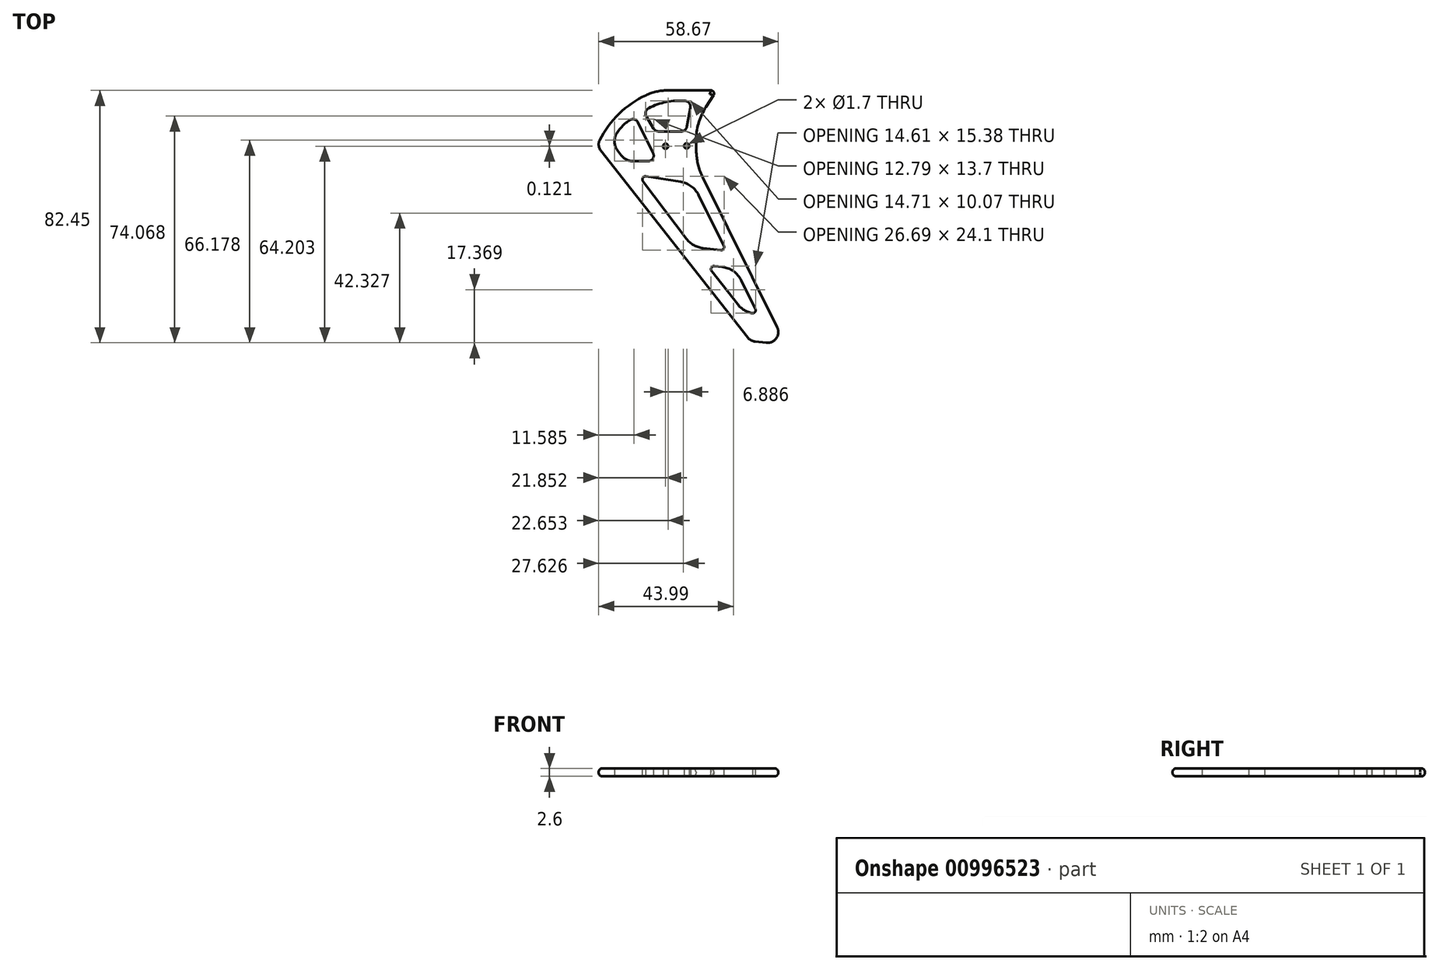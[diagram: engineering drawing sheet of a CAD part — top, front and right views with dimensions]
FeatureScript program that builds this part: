
annotation { "Feature Type Name" : "Feature", "Feature Type Description" : "" }
export const myFeature = defineFeature(function(context is Context, id is Id, definition is map)
    precondition{}
    {
        {
            var Q0;
            Q0=qCreatedBy(makeId("Top.planeOp"),FACE);
            var sketch = newSketch(context, id + "F0", { "sketchPlane" : qUnion([Q0])});
            skLineSegment(sketch, "E0", {"start": v(-19.01, 21.64) * mm, "end": v(31.12, -42.18) * mm});
            skLineSegment(sketch, "E1", {"start": v(31.12, -42.18) * mm, "end": v(42.66, -43.43) * mm});
            skLineSegment(sketch, "E2", {"start": v(42.66, -43.43) * mm, "end": v(14.03, 14.28) * mm});
            skArc(sketch, "E3", {"start": v(14.03, 30.36) * mm, "mid": v(13.3, 22.32) * mm, "end": v(14.03, 14.28) * mm});
            skLineSegment(sketch, "E4", {"start": v(20.02, 39.69) * mm, "end": v(0.9, 39.69) * mm});
            skArc(sketch, "E5", {"start": v(0.9, 39.69) * mm, "mid": v(-11, 32.8) * mm, "end": v(-19.01, 21.64) * mm});
            skLineSegment(sketch, "E6", {"start": v(20.02, 39.69) * mm, "end": v(14.03, 30.36) * mm});
            skLineSegment(sketch, "E7", {"start": v(26.15, -18.44) * mm, "end": v(33.42, -33.08) * mm});
            skLineSegment(sketch, "E8", {"start": v(33.42, -33.08) * mm, "end": v(29.2, -33.08) * mm});
            skLineSegment(sketch, "E9", {"start": v(29.2, -33.08) * mm, "end": v(16.91, -17.44) * mm});
            skLineSegment(sketch, "E10", {"start": v(16.91, -17.44) * mm, "end": v(26.15, -18.44) * mm});
            skLineSegment(sketch, "E11", {"start": v(12.26, -11.5) * mm, "end": v(23.19, -12.68) * mm});
            skLineSegment(sketch, "E12", {"start": v(23.19, -12.68) * mm, "end": v(12.34, 9.19) * mm});
            skLineSegment(sketch, "E13", {"start": v(12.34, 9.19) * mm, "end": v(-5.53, 12) * mm});
            skLineSegment(sketch, "E14", {"start": v(-5.53, 12) * mm, "end": v(12.26, -11.5) * mm});
            skLineSegment(sketch, "E15", {"start": v(-6.51, 30.94) * mm, "end": v(0.62, 16.57) * mm});
            skLineSegment(sketch, "E16", {"start": v(0.62, 16.57) * mm, "end": v(-9.65, 16.57) * mm});
            skLineSegment(sketch, "E17", {"start": v(-9.65, 16.57) * mm, "end": v(-14.05, 22.38) * mm});
            skArc(sketch, "E18", {"start": v(-6.51, 30.94) * mm, "mid": v(-11.24, 27.5) * mm, "end": v(-14.05, 22.38) * mm});
            skLineSegment(sketch, "E19", {"start": v(10.04, 26.27) * mm, "end": v(0, 26.27) * mm});
            skLineSegment(sketch, "E20", {"start": v(0, 26.27) * mm, "end": v(-3.94, 32.84) * mm});
            skLineSegment(sketch, "E21", {"start": v(10.04, 26.27) * mm, "end": v(11.85, 35.98) * mm});
            skArc(sketch, "E22", {"start": v(11.85, 35.98) * mm, "mid": v(3.65, 35.93) * mm, "end": v(-3.94, 32.84) * mm});
            skCircle(sketch, "E23", {"center": v(3.35, 21.44) * mm, "radius": 0.85 * mm});
            skCircle(sketch, "E24", {"center": v(10.24, 21.56) * mm, "radius": 0.85 * mm});
            skSolve(sketch);
        }
        {
            var Q0;
            Q0=makeQuery(id+"F0.imprint","IMPRINT",FACE,{"disambiguationData":[TD([[makeQuery(id+"F0.imprint","IMPRINT",EDGE,{"derivedFrom":sQuery(id+"F0.wireOp",EDGE,"E0")}),1.0]])]});
            extrude(context, id + "F1", {"entities" : qUnion([Q0]), "depth" : 2.6 * mm, "offsetDistance" : 25 * mm});
        }
        {
            var Q0;
            Q0=makeQuery(id+"F1.opExtrude","SWEPT_EDGE",EDGE,{"disambiguationData":[OSD([sQuery(id+"F0.wireOp",EDGE,"E4"),sQuery(id+"F0.wireOp",EDGE,"E6")])]});
            fillet(context, id + "F2", {"entities" : qUnion([Q0]), "radius" : 1.01 * mm, "tangentPropagation" : true, "allowEdgeOverflow" : false});
        }
        {
            var Q0;
            Q0=makeQuery(id+"F1.opExtrude","SWEPT_EDGE",EDGE,{"disambiguationData":[OSD([sQuery(id+"F0.wireOp",EDGE,"E20"),sQuery(id+"F0.wireOp",EDGE,"E22")])]});
            var Q1;
            Q1=makeQuery(id+"F1.opExtrude","SWEPT_EDGE",EDGE,{"disambiguationData":[OSD([sQuery(id+"F0.wireOp",EDGE,"E21"),sQuery(id+"F0.wireOp",EDGE,"E22")])]});
            var Q2;
            Q2=makeQuery(id+"F1.opExtrude","SWEPT_EDGE",EDGE,{"disambiguationData":[OSD([sQuery(id+"F0.wireOp",EDGE,"E19"),sQuery(id+"F0.wireOp",EDGE,"E21")])]});
            var Q3;
            Q3=makeQuery(id+"F1.opExtrude","SWEPT_EDGE",EDGE,{"disambiguationData":[OSD([sQuery(id+"F0.wireOp",EDGE,"E19"),sQuery(id+"F0.wireOp",EDGE,"E20")])]});
            fillet(context, id + "F3", {"entities" : qUnion([Q0, Q1, Q2, Q3]), "radius" : 1.95 * mm, "tangentPropagation" : true, "allowEdgeOverflow" : false});
        }
        {
            var Q0;
            Q0=makeQuery(id+"F1.opExtrude","SWEPT_EDGE",EDGE,{"disambiguationData":[OSD([sQuery(id+"F0.wireOp",EDGE,"E13"),sQuery(id+"F0.wireOp",EDGE,"E14")])]});
            var Q1;
            Q1=makeQuery(id+"F1.opExtrude","SWEPT_EDGE",EDGE,{"disambiguationData":[OSD([sQuery(id+"F0.wireOp",EDGE,"E7"),sQuery(id+"F0.wireOp",EDGE,"E8")])]});
            var Q2;
            Q2=makeQuery(id+"F1.opExtrude","SWEPT_EDGE",EDGE,{"disambiguationData":[OSD([sQuery(id+"F0.wireOp",EDGE,"E11"),sQuery(id+"F0.wireOp",EDGE,"E12")])]});
            var Q3;
            Q3=makeQuery(id+"F1.opExtrude","SWEPT_EDGE",EDGE,{"disambiguationData":[OSD([sQuery(id+"F0.wireOp",EDGE,"E9"),sQuery(id+"F0.wireOp",EDGE,"E10")])]});
            fillet(context, id + "F4", {"entities" : qUnion([Q0, Q1, Q2, Q3]), "radius" : 1.01 * mm, "tangentPropagation" : true, "allowEdgeOverflow" : false});
        }
        {
            var Q0;
            Q0=makeQuery(id+"F1.opExtrude","SWEPT_EDGE",EDGE,{"disambiguationData":[OSD([sQuery(id+"F0.wireOp",EDGE,"E7"),sQuery(id+"F0.wireOp",EDGE,"E10")])]});
            var Q1;
            Q1=makeQuery(id+"F1.opExtrude","SWEPT_EDGE",EDGE,{"disambiguationData":[OSD([sQuery(id+"F0.wireOp",EDGE,"E8"),sQuery(id+"F0.wireOp",EDGE,"E9")])]});
            var Q2;
            Q2=makeQuery(id+"F1.opExtrude","SWEPT_EDGE",EDGE,{"disambiguationData":[OSD([sQuery(id+"F0.wireOp",EDGE,"E11"),sQuery(id+"F0.wireOp",EDGE,"E14")])]});
            var Q3;
            Q3=makeQuery(id+"F1.opExtrude","SWEPT_EDGE",EDGE,{"disambiguationData":[OSD([sQuery(id+"F0.wireOp",EDGE,"E12"),sQuery(id+"F0.wireOp",EDGE,"E13")])]});
            fillet(context, id + "F5", {"entities" : qUnion([Q0, Q1, Q2, Q3]), "radius" : 7.96 * mm, "tangentPropagation" : true, "allowEdgeOverflow" : false});
        }
        {
            var Q0;
            Q0=makeQuery(id+"F1.opExtrude","SWEPT_EDGE",EDGE,{"disambiguationData":[OSD([sQuery(id+"F0.wireOp",EDGE,"E15"),sQuery(id+"F0.wireOp",EDGE,"E16")])]});
            var Q1;
            Q1=makeQuery(id+"F1.opExtrude","SWEPT_EDGE",EDGE,{"disambiguationData":[OSD([sQuery(id+"F0.wireOp",EDGE,"E15"),sQuery(id+"F0.wireOp",EDGE,"E18")])]});
            fillet(context, id + "F6", {"entities" : qUnion([Q0, Q1]), "radius" : 1.85 * mm, "tangentPropagation" : true, "allowEdgeOverflow" : false});
        }
        {
            var Q0;
            Q0=makeQuery(id+"F1.opExtrude","SWEPT_EDGE",EDGE,{"disambiguationData":[OSD([sQuery(id+"F0.wireOp",EDGE,"E16"),sQuery(id+"F0.wireOp",EDGE,"E17")])]});
            var Q1;
            Q1=makeQuery(id+"F1.opExtrude","SWEPT_EDGE",EDGE,{"disambiguationData":[OSD([sQuery(id+"F0.wireOp",EDGE,"E17"),sQuery(id+"F0.wireOp",EDGE,"E18")])]});
            fillet(context, id + "F7", {"entities" : qUnion([Q0, Q1]), "radius" : 5 * mm, "tangentPropagation" : true, "allowEdgeOverflow" : false});
        }
        {
            var Q0;
            Q0=makeQuery(id+"F1.opExtrude","SWEPT_EDGE",EDGE,{"disambiguationData":[OSD([sQuery(id+"F0.wireOp",EDGE,"E1"),sQuery(id+"F0.wireOp",EDGE,"E2")])]});
            var Q1;
            Q1=makeQuery(id+"F1.opExtrude","SWEPT_EDGE",EDGE,{"disambiguationData":[OSD([sQuery(id+"F0.wireOp",EDGE,"E0"),sQuery(id+"F0.wireOp",EDGE,"E1")])]});
            fillet(context, id + "F8", {"entities" : qUnion([Q0, Q1]), "radius" : 3.52 * mm, "tangentPropagation" : true, "allowEdgeOverflow" : false});
        }
        {
            var Q0;
            Q0=makeQuery(id+"F1.opExtrude","SWEPT_EDGE",EDGE,{"disambiguationData":[OSD([sQuery(id+"F0.wireOp",EDGE,"E0"),sQuery(id+"F0.wireOp",EDGE,"E5")])]});
            fillet(context, id + "F9", {"entities" : qUnion([Q0]), "radius" : 3.04 * mm, "tangentPropagation" : true, "allowEdgeOverflow" : false});
        }
        {
            var Q0;
            Q0=makeQuery(id+"F1.opExtrude","SWEPT_EDGE",EDGE,{"disambiguationData":[OSD([sQuery(id+"F0.wireOp",EDGE,"E4"),sQuery(id+"F0.wireOp",EDGE,"E5")])]});
            fillet(context, id + "F10", {"entities" : qUnion([Q0]), "radius" : 16.24 * mm, "tangentPropagation" : true, "allowEdgeOverflow" : false});
        }
        {
            var Q0;
            Q0=makeQuery(id+"F1.opExtrude","SWEPT_EDGE",EDGE,{"disambiguationData":[OSD([sQuery(id+"F0.wireOp",EDGE,"E3"),sQuery(id+"F0.wireOp",EDGE,"E6")])]});
            var Q1;
            Q1=makeQuery(id+"F1.opExtrude","SWEPT_EDGE",EDGE,{"disambiguationData":[OSD([sQuery(id+"F0.wireOp",EDGE,"E2"),sQuery(id+"F0.wireOp",EDGE,"E3")])]});
            fillet(context, id + "F11", {"entities" : qUnion([Q0, Q1]), "radius" : 20.3 * mm, "tangentPropagation" : true, "allowEdgeOverflow" : false});
        }
        {
            var Q0;
            {var subQ0=sQuery(id+"F0.wireOp",EDGE,"E2");var subQ1=sQuery(id+"F0.wireOp",EDGE,"E1");Q0=makeQuery(id+"F8.opFillet","BLEND_EDGE",EDGE,{"blendedFrom":[makeQuery(id+"F1.opExtrude","SWEPT_EDGE",EDGE,{"disambiguationData":[OSD([subQ1,subQ0])]}),makeQuery(id+"F1.opExtrude","CAP_FACE",FACE,{"disambiguationData":[OSD([sQuery(id+"F0.wireOp",EDGE,"E0"),subQ1,subQ0,sQuery(id+"F0.wireOp",EDGE,"E3"),sQuery(id+"F0.wireOp",EDGE,"E4"),sQuery(id+"F0.wireOp",EDGE,"E5"),sQuery(id+"F0.wireOp",EDGE,"E6"),sQuery(id+"F0.wireOp",EDGE,"E7"),sQuery(id+"F0.wireOp",EDGE,"E8"),sQuery(id+"F0.wireOp",EDGE,"E9"),sQuery(id+"F0.wireOp",EDGE,"E10"),sQuery(id+"F0.wireOp",EDGE,"E11"),sQuery(id+"F0.wireOp",EDGE,"E12"),sQuery(id+"F0.wireOp",EDGE,"E13"),sQuery(id+"F0.wireOp",EDGE,"E14"),sQuery(id+"F0.wireOp",EDGE,"E15"),sQuery(id+"F0.wireOp",EDGE,"E16"),sQuery(id+"F0.wireOp",EDGE,"E17"),sQuery(id+"F0.wireOp",EDGE,"E18"),sQuery(id+"F0.wireOp",EDGE,"E19"),sQuery(id+"F0.wireOp",EDGE,"E20"),sQuery(id+"F0.wireOp",EDGE,"E21"),sQuery(id+"F0.wireOp",EDGE,"E22"),sQuery(id+"F0.wireOp",EDGE,"E23"),sQuery(id+"F0.wireOp",EDGE,"E24")])],"isStart":false})],"blendedInto":[makeQuery(id+"F1.opExtrude","CAP_FACE",FACE,{"disambiguationData":[OSD([sQuery(id+"F0.wireOp",EDGE,"E0"),subQ1,subQ0,sQuery(id+"F0.wireOp",EDGE,"E3"),sQuery(id+"F0.wireOp",EDGE,"E4"),sQuery(id+"F0.wireOp",EDGE,"E5"),sQuery(id+"F0.wireOp",EDGE,"E6"),sQuery(id+"F0.wireOp",EDGE,"E7"),sQuery(id+"F0.wireOp",EDGE,"E8"),sQuery(id+"F0.wireOp",EDGE,"E9"),sQuery(id+"F0.wireOp",EDGE,"E10"),sQuery(id+"F0.wireOp",EDGE,"E11"),sQuery(id+"F0.wireOp",EDGE,"E12"),sQuery(id+"F0.wireOp",EDGE,"E13"),sQuery(id+"F0.wireOp",EDGE,"E14"),sQuery(id+"F0.wireOp",EDGE,"E15"),sQuery(id+"F0.wireOp",EDGE,"E16"),sQuery(id+"F0.wireOp",EDGE,"E17"),sQuery(id+"F0.wireOp",EDGE,"E18"),sQuery(id+"F0.wireOp",EDGE,"E19"),sQuery(id+"F0.wireOp",EDGE,"E20"),sQuery(id+"F0.wireOp",EDGE,"E21"),sQuery(id+"F0.wireOp",EDGE,"E22"),sQuery(id+"F0.wireOp",EDGE,"E23"),sQuery(id+"F0.wireOp",EDGE,"E24")])],"isStart":false})]});}
            var Q1;
            {var subQ0=sQuery(id+"F0.wireOp",EDGE,"E2");var subQ1=sQuery(id+"F0.wireOp",EDGE,"E1");Q1=makeQuery(id+"F8.opFillet","BLEND_EDGE",EDGE,{"blendedFrom":[makeQuery(id+"F1.opExtrude","SWEPT_EDGE",EDGE,{"disambiguationData":[OSD([subQ1,subQ0])]}),makeQuery(id+"F1.opExtrude","CAP_FACE",FACE,{"disambiguationData":[OSD([sQuery(id+"F0.wireOp",EDGE,"E0"),subQ1,subQ0,sQuery(id+"F0.wireOp",EDGE,"E3"),sQuery(id+"F0.wireOp",EDGE,"E4"),sQuery(id+"F0.wireOp",EDGE,"E5"),sQuery(id+"F0.wireOp",EDGE,"E6"),sQuery(id+"F0.wireOp",EDGE,"E7"),sQuery(id+"F0.wireOp",EDGE,"E8"),sQuery(id+"F0.wireOp",EDGE,"E9"),sQuery(id+"F0.wireOp",EDGE,"E10"),sQuery(id+"F0.wireOp",EDGE,"E11"),sQuery(id+"F0.wireOp",EDGE,"E12"),sQuery(id+"F0.wireOp",EDGE,"E13"),sQuery(id+"F0.wireOp",EDGE,"E14"),sQuery(id+"F0.wireOp",EDGE,"E15"),sQuery(id+"F0.wireOp",EDGE,"E16"),sQuery(id+"F0.wireOp",EDGE,"E17"),sQuery(id+"F0.wireOp",EDGE,"E18"),sQuery(id+"F0.wireOp",EDGE,"E19"),sQuery(id+"F0.wireOp",EDGE,"E20"),sQuery(id+"F0.wireOp",EDGE,"E21"),sQuery(id+"F0.wireOp",EDGE,"E22"),sQuery(id+"F0.wireOp",EDGE,"E23"),sQuery(id+"F0.wireOp",EDGE,"E24")])],"isStart":true})],"blendedInto":[makeQuery(id+"F1.opExtrude","CAP_FACE",FACE,{"disambiguationData":[OSD([sQuery(id+"F0.wireOp",EDGE,"E0"),subQ1,subQ0,sQuery(id+"F0.wireOp",EDGE,"E3"),sQuery(id+"F0.wireOp",EDGE,"E4"),sQuery(id+"F0.wireOp",EDGE,"E5"),sQuery(id+"F0.wireOp",EDGE,"E6"),sQuery(id+"F0.wireOp",EDGE,"E7"),sQuery(id+"F0.wireOp",EDGE,"E8"),sQuery(id+"F0.wireOp",EDGE,"E9"),sQuery(id+"F0.wireOp",EDGE,"E10"),sQuery(id+"F0.wireOp",EDGE,"E11"),sQuery(id+"F0.wireOp",EDGE,"E12"),sQuery(id+"F0.wireOp",EDGE,"E13"),sQuery(id+"F0.wireOp",EDGE,"E14"),sQuery(id+"F0.wireOp",EDGE,"E15"),sQuery(id+"F0.wireOp",EDGE,"E16"),sQuery(id+"F0.wireOp",EDGE,"E17"),sQuery(id+"F0.wireOp",EDGE,"E18"),sQuery(id+"F0.wireOp",EDGE,"E19"),sQuery(id+"F0.wireOp",EDGE,"E20"),sQuery(id+"F0.wireOp",EDGE,"E21"),sQuery(id+"F0.wireOp",EDGE,"E22"),sQuery(id+"F0.wireOp",EDGE,"E23"),sQuery(id+"F0.wireOp",EDGE,"E24")])],"isStart":true})]});}
            var Q2;
            Q2=makeQuery(id+"F1.opExtrude","CAP_EDGE",EDGE,{"disambiguationData":[OSD([sQuery(id+"F0.wireOp",EDGE,"E1")])],"isStart":true});
            var Q3;
            Q3=makeQuery(id+"F1.opExtrude","CAP_EDGE",EDGE,{"disambiguationData":[OSD([sQuery(id+"F0.wireOp",EDGE,"E1")])],"isStart":false});
            var Q4;
            {var subQ0=sQuery(id+"F0.wireOp",EDGE,"E1");var subQ1=sQuery(id+"F0.wireOp",EDGE,"E0");Q4=makeQuery(id+"F8.opFillet","BLEND_EDGE",EDGE,{"blendedFrom":[makeQuery(id+"F1.opExtrude","SWEPT_EDGE",EDGE,{"disambiguationData":[OSD([subQ1,subQ0])]}),makeQuery(id+"F1.opExtrude","CAP_FACE",FACE,{"disambiguationData":[OSD([subQ1,subQ0,sQuery(id+"F0.wireOp",EDGE,"E2"),sQuery(id+"F0.wireOp",EDGE,"E3"),sQuery(id+"F0.wireOp",EDGE,"E4"),sQuery(id+"F0.wireOp",EDGE,"E5"),sQuery(id+"F0.wireOp",EDGE,"E6"),sQuery(id+"F0.wireOp",EDGE,"E7"),sQuery(id+"F0.wireOp",EDGE,"E8"),sQuery(id+"F0.wireOp",EDGE,"E9"),sQuery(id+"F0.wireOp",EDGE,"E10"),sQuery(id+"F0.wireOp",EDGE,"E11"),sQuery(id+"F0.wireOp",EDGE,"E12"),sQuery(id+"F0.wireOp",EDGE,"E13"),sQuery(id+"F0.wireOp",EDGE,"E14"),sQuery(id+"F0.wireOp",EDGE,"E15"),sQuery(id+"F0.wireOp",EDGE,"E16"),sQuery(id+"F0.wireOp",EDGE,"E17"),sQuery(id+"F0.wireOp",EDGE,"E18"),sQuery(id+"F0.wireOp",EDGE,"E19"),sQuery(id+"F0.wireOp",EDGE,"E20"),sQuery(id+"F0.wireOp",EDGE,"E21"),sQuery(id+"F0.wireOp",EDGE,"E22"),sQuery(id+"F0.wireOp",EDGE,"E23"),sQuery(id+"F0.wireOp",EDGE,"E24")])],"isStart":true})],"blendedInto":[makeQuery(id+"F1.opExtrude","CAP_FACE",FACE,{"disambiguationData":[OSD([subQ1,subQ0,sQuery(id+"F0.wireOp",EDGE,"E2"),sQuery(id+"F0.wireOp",EDGE,"E3"),sQuery(id+"F0.wireOp",EDGE,"E4"),sQuery(id+"F0.wireOp",EDGE,"E5"),sQuery(id+"F0.wireOp",EDGE,"E6"),sQuery(id+"F0.wireOp",EDGE,"E7"),sQuery(id+"F0.wireOp",EDGE,"E8"),sQuery(id+"F0.wireOp",EDGE,"E9"),sQuery(id+"F0.wireOp",EDGE,"E10"),sQuery(id+"F0.wireOp",EDGE,"E11"),sQuery(id+"F0.wireOp",EDGE,"E12"),sQuery(id+"F0.wireOp",EDGE,"E13"),sQuery(id+"F0.wireOp",EDGE,"E14"),sQuery(id+"F0.wireOp",EDGE,"E15"),sQuery(id+"F0.wireOp",EDGE,"E16"),sQuery(id+"F0.wireOp",EDGE,"E17"),sQuery(id+"F0.wireOp",EDGE,"E18"),sQuery(id+"F0.wireOp",EDGE,"E19"),sQuery(id+"F0.wireOp",EDGE,"E20"),sQuery(id+"F0.wireOp",EDGE,"E21"),sQuery(id+"F0.wireOp",EDGE,"E22"),sQuery(id+"F0.wireOp",EDGE,"E23"),sQuery(id+"F0.wireOp",EDGE,"E24")])],"isStart":true})]});}
            var Q5;
            {var subQ0=sQuery(id+"F0.wireOp",EDGE,"E1");var subQ1=sQuery(id+"F0.wireOp",EDGE,"E0");Q5=makeQuery(id+"F8.opFillet","BLEND_EDGE",EDGE,{"blendedFrom":[makeQuery(id+"F1.opExtrude","SWEPT_EDGE",EDGE,{"disambiguationData":[OSD([subQ1,subQ0])]}),makeQuery(id+"F1.opExtrude","CAP_FACE",FACE,{"disambiguationData":[OSD([subQ1,subQ0,sQuery(id+"F0.wireOp",EDGE,"E2"),sQuery(id+"F0.wireOp",EDGE,"E3"),sQuery(id+"F0.wireOp",EDGE,"E4"),sQuery(id+"F0.wireOp",EDGE,"E5"),sQuery(id+"F0.wireOp",EDGE,"E6"),sQuery(id+"F0.wireOp",EDGE,"E7"),sQuery(id+"F0.wireOp",EDGE,"E8"),sQuery(id+"F0.wireOp",EDGE,"E9"),sQuery(id+"F0.wireOp",EDGE,"E10"),sQuery(id+"F0.wireOp",EDGE,"E11"),sQuery(id+"F0.wireOp",EDGE,"E12"),sQuery(id+"F0.wireOp",EDGE,"E13"),sQuery(id+"F0.wireOp",EDGE,"E14"),sQuery(id+"F0.wireOp",EDGE,"E15"),sQuery(id+"F0.wireOp",EDGE,"E16"),sQuery(id+"F0.wireOp",EDGE,"E17"),sQuery(id+"F0.wireOp",EDGE,"E18"),sQuery(id+"F0.wireOp",EDGE,"E19"),sQuery(id+"F0.wireOp",EDGE,"E20"),sQuery(id+"F0.wireOp",EDGE,"E21"),sQuery(id+"F0.wireOp",EDGE,"E22"),sQuery(id+"F0.wireOp",EDGE,"E23"),sQuery(id+"F0.wireOp",EDGE,"E24")])],"isStart":false})],"blendedInto":[makeQuery(id+"F1.opExtrude","CAP_FACE",FACE,{"disambiguationData":[OSD([subQ1,subQ0,sQuery(id+"F0.wireOp",EDGE,"E2"),sQuery(id+"F0.wireOp",EDGE,"E3"),sQuery(id+"F0.wireOp",EDGE,"E4"),sQuery(id+"F0.wireOp",EDGE,"E5"),sQuery(id+"F0.wireOp",EDGE,"E6"),sQuery(id+"F0.wireOp",EDGE,"E7"),sQuery(id+"F0.wireOp",EDGE,"E8"),sQuery(id+"F0.wireOp",EDGE,"E9"),sQuery(id+"F0.wireOp",EDGE,"E10"),sQuery(id+"F0.wireOp",EDGE,"E11"),sQuery(id+"F0.wireOp",EDGE,"E12"),sQuery(id+"F0.wireOp",EDGE,"E13"),sQuery(id+"F0.wireOp",EDGE,"E14"),sQuery(id+"F0.wireOp",EDGE,"E15"),sQuery(id+"F0.wireOp",EDGE,"E16"),sQuery(id+"F0.wireOp",EDGE,"E17"),sQuery(id+"F0.wireOp",EDGE,"E18"),sQuery(id+"F0.wireOp",EDGE,"E19"),sQuery(id+"F0.wireOp",EDGE,"E20"),sQuery(id+"F0.wireOp",EDGE,"E21"),sQuery(id+"F0.wireOp",EDGE,"E22"),sQuery(id+"F0.wireOp",EDGE,"E23"),sQuery(id+"F0.wireOp",EDGE,"E24")])],"isStart":false})]});}
            var Q6;
            Q6=makeQuery(id+"F1.opExtrude","CAP_EDGE",EDGE,{"disambiguationData":[OSD([sQuery(id+"F0.wireOp",EDGE,"E0")])],"isStart":true});
            var Q7;
            Q7=makeQuery(id+"F1.opExtrude","CAP_EDGE",EDGE,{"disambiguationData":[OSD([sQuery(id+"F0.wireOp",EDGE,"E0")])],"isStart":false});
            var Q8;
            Q8=makeQuery(id+"F1.opExtrude","CAP_EDGE",EDGE,{"disambiguationData":[OSD([sQuery(id+"F0.wireOp",EDGE,"E2")])],"isStart":true});
            var Q9;
            Q9=makeQuery(id+"F1.opExtrude","CAP_EDGE",EDGE,{"disambiguationData":[OSD([sQuery(id+"F0.wireOp",EDGE,"E2")])],"isStart":false});
            var Q10;
            {var subQ0=sQuery(id+"F0.wireOp",EDGE,"E3");var subQ1=sQuery(id+"F0.wireOp",EDGE,"E2");Q10=makeQuery(id+"F11.opFillet","BLEND_EDGE",EDGE,{"blendedFrom":[makeQuery(id+"F1.opExtrude","SWEPT_EDGE",EDGE,{"disambiguationData":[OSD([subQ1,subQ0])]}),makeQuery(id+"F1.opExtrude","CAP_FACE",FACE,{"disambiguationData":[OSD([sQuery(id+"F0.wireOp",EDGE,"E0"),sQuery(id+"F0.wireOp",EDGE,"E1"),subQ1,subQ0,sQuery(id+"F0.wireOp",EDGE,"E4"),sQuery(id+"F0.wireOp",EDGE,"E5"),sQuery(id+"F0.wireOp",EDGE,"E6"),sQuery(id+"F0.wireOp",EDGE,"E7"),sQuery(id+"F0.wireOp",EDGE,"E8"),sQuery(id+"F0.wireOp",EDGE,"E9"),sQuery(id+"F0.wireOp",EDGE,"E10"),sQuery(id+"F0.wireOp",EDGE,"E11"),sQuery(id+"F0.wireOp",EDGE,"E12"),sQuery(id+"F0.wireOp",EDGE,"E13"),sQuery(id+"F0.wireOp",EDGE,"E14"),sQuery(id+"F0.wireOp",EDGE,"E15"),sQuery(id+"F0.wireOp",EDGE,"E16"),sQuery(id+"F0.wireOp",EDGE,"E17"),sQuery(id+"F0.wireOp",EDGE,"E18"),sQuery(id+"F0.wireOp",EDGE,"E19"),sQuery(id+"F0.wireOp",EDGE,"E20"),sQuery(id+"F0.wireOp",EDGE,"E21"),sQuery(id+"F0.wireOp",EDGE,"E22"),sQuery(id+"F0.wireOp",EDGE,"E23"),sQuery(id+"F0.wireOp",EDGE,"E24")])],"isStart":true})],"blendedInto":[makeQuery(id+"F1.opExtrude","CAP_FACE",FACE,{"disambiguationData":[OSD([sQuery(id+"F0.wireOp",EDGE,"E0"),sQuery(id+"F0.wireOp",EDGE,"E1"),subQ1,subQ0,sQuery(id+"F0.wireOp",EDGE,"E4"),sQuery(id+"F0.wireOp",EDGE,"E5"),sQuery(id+"F0.wireOp",EDGE,"E6"),sQuery(id+"F0.wireOp",EDGE,"E7"),sQuery(id+"F0.wireOp",EDGE,"E8"),sQuery(id+"F0.wireOp",EDGE,"E9"),sQuery(id+"F0.wireOp",EDGE,"E10"),sQuery(id+"F0.wireOp",EDGE,"E11"),sQuery(id+"F0.wireOp",EDGE,"E12"),sQuery(id+"F0.wireOp",EDGE,"E13"),sQuery(id+"F0.wireOp",EDGE,"E14"),sQuery(id+"F0.wireOp",EDGE,"E15"),sQuery(id+"F0.wireOp",EDGE,"E16"),sQuery(id+"F0.wireOp",EDGE,"E17"),sQuery(id+"F0.wireOp",EDGE,"E18"),sQuery(id+"F0.wireOp",EDGE,"E19"),sQuery(id+"F0.wireOp",EDGE,"E20"),sQuery(id+"F0.wireOp",EDGE,"E21"),sQuery(id+"F0.wireOp",EDGE,"E22"),sQuery(id+"F0.wireOp",EDGE,"E23"),sQuery(id+"F0.wireOp",EDGE,"E24")])],"isStart":true})]});}
            var Q11;
            {var subQ0=sQuery(id+"F0.wireOp",EDGE,"E3");var subQ1=sQuery(id+"F0.wireOp",EDGE,"E2");Q11=makeQuery(id+"F11.opFillet","BLEND_EDGE",EDGE,{"blendedFrom":[makeQuery(id+"F1.opExtrude","SWEPT_EDGE",EDGE,{"disambiguationData":[OSD([subQ1,subQ0])]}),makeQuery(id+"F1.opExtrude","CAP_FACE",FACE,{"disambiguationData":[OSD([sQuery(id+"F0.wireOp",EDGE,"E0"),sQuery(id+"F0.wireOp",EDGE,"E1"),subQ1,subQ0,sQuery(id+"F0.wireOp",EDGE,"E4"),sQuery(id+"F0.wireOp",EDGE,"E5"),sQuery(id+"F0.wireOp",EDGE,"E6"),sQuery(id+"F0.wireOp",EDGE,"E7"),sQuery(id+"F0.wireOp",EDGE,"E8"),sQuery(id+"F0.wireOp",EDGE,"E9"),sQuery(id+"F0.wireOp",EDGE,"E10"),sQuery(id+"F0.wireOp",EDGE,"E11"),sQuery(id+"F0.wireOp",EDGE,"E12"),sQuery(id+"F0.wireOp",EDGE,"E13"),sQuery(id+"F0.wireOp",EDGE,"E14"),sQuery(id+"F0.wireOp",EDGE,"E15"),sQuery(id+"F0.wireOp",EDGE,"E16"),sQuery(id+"F0.wireOp",EDGE,"E17"),sQuery(id+"F0.wireOp",EDGE,"E18"),sQuery(id+"F0.wireOp",EDGE,"E19"),sQuery(id+"F0.wireOp",EDGE,"E20"),sQuery(id+"F0.wireOp",EDGE,"E21"),sQuery(id+"F0.wireOp",EDGE,"E22"),sQuery(id+"F0.wireOp",EDGE,"E23"),sQuery(id+"F0.wireOp",EDGE,"E24")])],"isStart":false})],"blendedInto":[makeQuery(id+"F1.opExtrude","CAP_FACE",FACE,{"disambiguationData":[OSD([sQuery(id+"F0.wireOp",EDGE,"E0"),sQuery(id+"F0.wireOp",EDGE,"E1"),subQ1,subQ0,sQuery(id+"F0.wireOp",EDGE,"E4"),sQuery(id+"F0.wireOp",EDGE,"E5"),sQuery(id+"F0.wireOp",EDGE,"E6"),sQuery(id+"F0.wireOp",EDGE,"E7"),sQuery(id+"F0.wireOp",EDGE,"E8"),sQuery(id+"F0.wireOp",EDGE,"E9"),sQuery(id+"F0.wireOp",EDGE,"E10"),sQuery(id+"F0.wireOp",EDGE,"E11"),sQuery(id+"F0.wireOp",EDGE,"E12"),sQuery(id+"F0.wireOp",EDGE,"E13"),sQuery(id+"F0.wireOp",EDGE,"E14"),sQuery(id+"F0.wireOp",EDGE,"E15"),sQuery(id+"F0.wireOp",EDGE,"E16"),sQuery(id+"F0.wireOp",EDGE,"E17"),sQuery(id+"F0.wireOp",EDGE,"E18"),sQuery(id+"F0.wireOp",EDGE,"E19"),sQuery(id+"F0.wireOp",EDGE,"E20"),sQuery(id+"F0.wireOp",EDGE,"E21"),sQuery(id+"F0.wireOp",EDGE,"E22"),sQuery(id+"F0.wireOp",EDGE,"E23"),sQuery(id+"F0.wireOp",EDGE,"E24")])],"isStart":false})]});}
            var Q12;
            Q12=makeQuery(id+"F1.opExtrude","CAP_EDGE",EDGE,{"disambiguationData":[OSD([sQuery(id+"F0.wireOp",EDGE,"E3")])],"isStart":false});
            var Q13;
            Q13=makeQuery(id+"F1.opExtrude","CAP_EDGE",EDGE,{"disambiguationData":[OSD([sQuery(id+"F0.wireOp",EDGE,"E3")])],"isStart":true});
            var Q14;
            {var subQ0=sQuery(id+"F0.wireOp",EDGE,"E6");var subQ1=sQuery(id+"F0.wireOp",EDGE,"E3");Q14=makeQuery(id+"F11.opFillet","BLEND_EDGE",EDGE,{"blendedFrom":[makeQuery(id+"F1.opExtrude","SWEPT_EDGE",EDGE,{"disambiguationData":[OSD([subQ1,subQ0])]}),makeQuery(id+"F1.opExtrude","CAP_FACE",FACE,{"disambiguationData":[OSD([sQuery(id+"F0.wireOp",EDGE,"E0"),sQuery(id+"F0.wireOp",EDGE,"E1"),sQuery(id+"F0.wireOp",EDGE,"E2"),subQ1,sQuery(id+"F0.wireOp",EDGE,"E4"),sQuery(id+"F0.wireOp",EDGE,"E5"),subQ0,sQuery(id+"F0.wireOp",EDGE,"E7"),sQuery(id+"F0.wireOp",EDGE,"E8"),sQuery(id+"F0.wireOp",EDGE,"E9"),sQuery(id+"F0.wireOp",EDGE,"E10"),sQuery(id+"F0.wireOp",EDGE,"E11"),sQuery(id+"F0.wireOp",EDGE,"E12"),sQuery(id+"F0.wireOp",EDGE,"E13"),sQuery(id+"F0.wireOp",EDGE,"E14"),sQuery(id+"F0.wireOp",EDGE,"E15"),sQuery(id+"F0.wireOp",EDGE,"E16"),sQuery(id+"F0.wireOp",EDGE,"E17"),sQuery(id+"F0.wireOp",EDGE,"E18"),sQuery(id+"F0.wireOp",EDGE,"E19"),sQuery(id+"F0.wireOp",EDGE,"E20"),sQuery(id+"F0.wireOp",EDGE,"E21"),sQuery(id+"F0.wireOp",EDGE,"E22"),sQuery(id+"F0.wireOp",EDGE,"E23"),sQuery(id+"F0.wireOp",EDGE,"E24")])],"isStart":true})],"blendedInto":[makeQuery(id+"F1.opExtrude","CAP_FACE",FACE,{"disambiguationData":[OSD([sQuery(id+"F0.wireOp",EDGE,"E0"),sQuery(id+"F0.wireOp",EDGE,"E1"),sQuery(id+"F0.wireOp",EDGE,"E2"),subQ1,sQuery(id+"F0.wireOp",EDGE,"E4"),sQuery(id+"F0.wireOp",EDGE,"E5"),subQ0,sQuery(id+"F0.wireOp",EDGE,"E7"),sQuery(id+"F0.wireOp",EDGE,"E8"),sQuery(id+"F0.wireOp",EDGE,"E9"),sQuery(id+"F0.wireOp",EDGE,"E10"),sQuery(id+"F0.wireOp",EDGE,"E11"),sQuery(id+"F0.wireOp",EDGE,"E12"),sQuery(id+"F0.wireOp",EDGE,"E13"),sQuery(id+"F0.wireOp",EDGE,"E14"),sQuery(id+"F0.wireOp",EDGE,"E15"),sQuery(id+"F0.wireOp",EDGE,"E16"),sQuery(id+"F0.wireOp",EDGE,"E17"),sQuery(id+"F0.wireOp",EDGE,"E18"),sQuery(id+"F0.wireOp",EDGE,"E19"),sQuery(id+"F0.wireOp",EDGE,"E20"),sQuery(id+"F0.wireOp",EDGE,"E21"),sQuery(id+"F0.wireOp",EDGE,"E22"),sQuery(id+"F0.wireOp",EDGE,"E23"),sQuery(id+"F0.wireOp",EDGE,"E24")])],"isStart":true})]});}
            var Q15;
            {var subQ0=sQuery(id+"F0.wireOp",EDGE,"E6");var subQ1=sQuery(id+"F0.wireOp",EDGE,"E3");Q15=makeQuery(id+"F11.opFillet","BLEND_EDGE",EDGE,{"blendedFrom":[makeQuery(id+"F1.opExtrude","SWEPT_EDGE",EDGE,{"disambiguationData":[OSD([subQ1,subQ0])]}),makeQuery(id+"F1.opExtrude","CAP_FACE",FACE,{"disambiguationData":[OSD([sQuery(id+"F0.wireOp",EDGE,"E0"),sQuery(id+"F0.wireOp",EDGE,"E1"),sQuery(id+"F0.wireOp",EDGE,"E2"),subQ1,sQuery(id+"F0.wireOp",EDGE,"E4"),sQuery(id+"F0.wireOp",EDGE,"E5"),subQ0,sQuery(id+"F0.wireOp",EDGE,"E7"),sQuery(id+"F0.wireOp",EDGE,"E8"),sQuery(id+"F0.wireOp",EDGE,"E9"),sQuery(id+"F0.wireOp",EDGE,"E10"),sQuery(id+"F0.wireOp",EDGE,"E11"),sQuery(id+"F0.wireOp",EDGE,"E12"),sQuery(id+"F0.wireOp",EDGE,"E13"),sQuery(id+"F0.wireOp",EDGE,"E14"),sQuery(id+"F0.wireOp",EDGE,"E15"),sQuery(id+"F0.wireOp",EDGE,"E16"),sQuery(id+"F0.wireOp",EDGE,"E17"),sQuery(id+"F0.wireOp",EDGE,"E18"),sQuery(id+"F0.wireOp",EDGE,"E19"),sQuery(id+"F0.wireOp",EDGE,"E20"),sQuery(id+"F0.wireOp",EDGE,"E21"),sQuery(id+"F0.wireOp",EDGE,"E22"),sQuery(id+"F0.wireOp",EDGE,"E23"),sQuery(id+"F0.wireOp",EDGE,"E24")])],"isStart":false})],"blendedInto":[makeQuery(id+"F1.opExtrude","CAP_FACE",FACE,{"disambiguationData":[OSD([sQuery(id+"F0.wireOp",EDGE,"E0"),sQuery(id+"F0.wireOp",EDGE,"E1"),sQuery(id+"F0.wireOp",EDGE,"E2"),subQ1,sQuery(id+"F0.wireOp",EDGE,"E4"),sQuery(id+"F0.wireOp",EDGE,"E5"),subQ0,sQuery(id+"F0.wireOp",EDGE,"E7"),sQuery(id+"F0.wireOp",EDGE,"E8"),sQuery(id+"F0.wireOp",EDGE,"E9"),sQuery(id+"F0.wireOp",EDGE,"E10"),sQuery(id+"F0.wireOp",EDGE,"E11"),sQuery(id+"F0.wireOp",EDGE,"E12"),sQuery(id+"F0.wireOp",EDGE,"E13"),sQuery(id+"F0.wireOp",EDGE,"E14"),sQuery(id+"F0.wireOp",EDGE,"E15"),sQuery(id+"F0.wireOp",EDGE,"E16"),sQuery(id+"F0.wireOp",EDGE,"E17"),sQuery(id+"F0.wireOp",EDGE,"E18"),sQuery(id+"F0.wireOp",EDGE,"E19"),sQuery(id+"F0.wireOp",EDGE,"E20"),sQuery(id+"F0.wireOp",EDGE,"E21"),sQuery(id+"F0.wireOp",EDGE,"E22"),sQuery(id+"F0.wireOp",EDGE,"E23"),sQuery(id+"F0.wireOp",EDGE,"E24")])],"isStart":false})]});}
            var Q16;
            Q16=makeQuery(id+"F1.opExtrude","CAP_EDGE",EDGE,{"disambiguationData":[OSD([sQuery(id+"F0.wireOp",EDGE,"E6")])],"isStart":false});
            var Q17;
            Q17=makeQuery(id+"F1.opExtrude","CAP_EDGE",EDGE,{"disambiguationData":[OSD([sQuery(id+"F0.wireOp",EDGE,"E6")])],"isStart":true});
            var Q18;
            {var subQ0=sQuery(id+"F0.wireOp",EDGE,"E6");var subQ1=sQuery(id+"F0.wireOp",EDGE,"E4");Q18=makeQuery(id+"F2.opFillet","BLEND_EDGE",EDGE,{"blendedFrom":[makeQuery(id+"F1.opExtrude","SWEPT_EDGE",EDGE,{"disambiguationData":[OSD([subQ1,subQ0])]}),makeQuery(id+"F1.opExtrude","CAP_FACE",FACE,{"disambiguationData":[OSD([sQuery(id+"F0.wireOp",EDGE,"E0"),sQuery(id+"F0.wireOp",EDGE,"E1"),sQuery(id+"F0.wireOp",EDGE,"E2"),sQuery(id+"F0.wireOp",EDGE,"E3"),subQ1,sQuery(id+"F0.wireOp",EDGE,"E5"),subQ0,sQuery(id+"F0.wireOp",EDGE,"E7"),sQuery(id+"F0.wireOp",EDGE,"E8"),sQuery(id+"F0.wireOp",EDGE,"E9"),sQuery(id+"F0.wireOp",EDGE,"E10"),sQuery(id+"F0.wireOp",EDGE,"E11"),sQuery(id+"F0.wireOp",EDGE,"E12"),sQuery(id+"F0.wireOp",EDGE,"E13"),sQuery(id+"F0.wireOp",EDGE,"E14"),sQuery(id+"F0.wireOp",EDGE,"E15"),sQuery(id+"F0.wireOp",EDGE,"E16"),sQuery(id+"F0.wireOp",EDGE,"E17"),sQuery(id+"F0.wireOp",EDGE,"E18"),sQuery(id+"F0.wireOp",EDGE,"E19"),sQuery(id+"F0.wireOp",EDGE,"E20"),sQuery(id+"F0.wireOp",EDGE,"E21"),sQuery(id+"F0.wireOp",EDGE,"E22"),sQuery(id+"F0.wireOp",EDGE,"E23"),sQuery(id+"F0.wireOp",EDGE,"E24")])],"isStart":true})],"blendedInto":[makeQuery(id+"F1.opExtrude","CAP_FACE",FACE,{"disambiguationData":[OSD([sQuery(id+"F0.wireOp",EDGE,"E0"),sQuery(id+"F0.wireOp",EDGE,"E1"),sQuery(id+"F0.wireOp",EDGE,"E2"),sQuery(id+"F0.wireOp",EDGE,"E3"),subQ1,sQuery(id+"F0.wireOp",EDGE,"E5"),subQ0,sQuery(id+"F0.wireOp",EDGE,"E7"),sQuery(id+"F0.wireOp",EDGE,"E8"),sQuery(id+"F0.wireOp",EDGE,"E9"),sQuery(id+"F0.wireOp",EDGE,"E10"),sQuery(id+"F0.wireOp",EDGE,"E11"),sQuery(id+"F0.wireOp",EDGE,"E12"),sQuery(id+"F0.wireOp",EDGE,"E13"),sQuery(id+"F0.wireOp",EDGE,"E14"),sQuery(id+"F0.wireOp",EDGE,"E15"),sQuery(id+"F0.wireOp",EDGE,"E16"),sQuery(id+"F0.wireOp",EDGE,"E17"),sQuery(id+"F0.wireOp",EDGE,"E18"),sQuery(id+"F0.wireOp",EDGE,"E19"),sQuery(id+"F0.wireOp",EDGE,"E20"),sQuery(id+"F0.wireOp",EDGE,"E21"),sQuery(id+"F0.wireOp",EDGE,"E22"),sQuery(id+"F0.wireOp",EDGE,"E23"),sQuery(id+"F0.wireOp",EDGE,"E24")])],"isStart":true})]});}
            var Q19;
            {var subQ0=sQuery(id+"F0.wireOp",EDGE,"E6");var subQ1=sQuery(id+"F0.wireOp",EDGE,"E4");Q19=makeQuery(id+"F2.opFillet","BLEND_EDGE",EDGE,{"blendedFrom":[makeQuery(id+"F1.opExtrude","SWEPT_EDGE",EDGE,{"disambiguationData":[OSD([subQ1,subQ0])]}),makeQuery(id+"F1.opExtrude","CAP_FACE",FACE,{"disambiguationData":[OSD([sQuery(id+"F0.wireOp",EDGE,"E0"),sQuery(id+"F0.wireOp",EDGE,"E1"),sQuery(id+"F0.wireOp",EDGE,"E2"),sQuery(id+"F0.wireOp",EDGE,"E3"),subQ1,sQuery(id+"F0.wireOp",EDGE,"E5"),subQ0,sQuery(id+"F0.wireOp",EDGE,"E7"),sQuery(id+"F0.wireOp",EDGE,"E8"),sQuery(id+"F0.wireOp",EDGE,"E9"),sQuery(id+"F0.wireOp",EDGE,"E10"),sQuery(id+"F0.wireOp",EDGE,"E11"),sQuery(id+"F0.wireOp",EDGE,"E12"),sQuery(id+"F0.wireOp",EDGE,"E13"),sQuery(id+"F0.wireOp",EDGE,"E14"),sQuery(id+"F0.wireOp",EDGE,"E15"),sQuery(id+"F0.wireOp",EDGE,"E16"),sQuery(id+"F0.wireOp",EDGE,"E17"),sQuery(id+"F0.wireOp",EDGE,"E18"),sQuery(id+"F0.wireOp",EDGE,"E19"),sQuery(id+"F0.wireOp",EDGE,"E20"),sQuery(id+"F0.wireOp",EDGE,"E21"),sQuery(id+"F0.wireOp",EDGE,"E22"),sQuery(id+"F0.wireOp",EDGE,"E23"),sQuery(id+"F0.wireOp",EDGE,"E24")])],"isStart":false})],"blendedInto":[makeQuery(id+"F1.opExtrude","CAP_FACE",FACE,{"disambiguationData":[OSD([sQuery(id+"F0.wireOp",EDGE,"E0"),sQuery(id+"F0.wireOp",EDGE,"E1"),sQuery(id+"F0.wireOp",EDGE,"E2"),sQuery(id+"F0.wireOp",EDGE,"E3"),subQ1,sQuery(id+"F0.wireOp",EDGE,"E5"),subQ0,sQuery(id+"F0.wireOp",EDGE,"E7"),sQuery(id+"F0.wireOp",EDGE,"E8"),sQuery(id+"F0.wireOp",EDGE,"E9"),sQuery(id+"F0.wireOp",EDGE,"E10"),sQuery(id+"F0.wireOp",EDGE,"E11"),sQuery(id+"F0.wireOp",EDGE,"E12"),sQuery(id+"F0.wireOp",EDGE,"E13"),sQuery(id+"F0.wireOp",EDGE,"E14"),sQuery(id+"F0.wireOp",EDGE,"E15"),sQuery(id+"F0.wireOp",EDGE,"E16"),sQuery(id+"F0.wireOp",EDGE,"E17"),sQuery(id+"F0.wireOp",EDGE,"E18"),sQuery(id+"F0.wireOp",EDGE,"E19"),sQuery(id+"F0.wireOp",EDGE,"E20"),sQuery(id+"F0.wireOp",EDGE,"E21"),sQuery(id+"F0.wireOp",EDGE,"E22"),sQuery(id+"F0.wireOp",EDGE,"E23"),sQuery(id+"F0.wireOp",EDGE,"E24")])],"isStart":false})]});}
            var Q20;
            Q20=makeQuery(id+"F1.opExtrude","CAP_EDGE",EDGE,{"disambiguationData":[OSD([sQuery(id+"F0.wireOp",EDGE,"E4")])],"isStart":false});
            var Q21;
            Q21=makeQuery(id+"F1.opExtrude","CAP_EDGE",EDGE,{"disambiguationData":[OSD([sQuery(id+"F0.wireOp",EDGE,"E4")])],"isStart":true});
            var Q22;
            Q22=makeQuery(id+"F1.opExtrude","CAP_EDGE",EDGE,{"disambiguationData":[OSD([sQuery(id+"F0.wireOp",EDGE,"E5")])],"isStart":true});
            var Q23;
            Q23=makeQuery(id+"F1.opExtrude","CAP_EDGE",EDGE,{"disambiguationData":[OSD([sQuery(id+"F0.wireOp",EDGE,"E5")])],"isStart":false});
            var Q24;
            {var subQ0=sQuery(id+"F0.wireOp",EDGE,"E5");var subQ1=sQuery(id+"F0.wireOp",EDGE,"E0");Q24=makeQuery(id+"F9.opFillet","BLEND_EDGE",EDGE,{"blendedFrom":[makeQuery(id+"F1.opExtrude","SWEPT_EDGE",EDGE,{"disambiguationData":[OSD([subQ1,subQ0])]}),makeQuery(id+"F1.opExtrude","CAP_FACE",FACE,{"disambiguationData":[OSD([subQ1,sQuery(id+"F0.wireOp",EDGE,"E1"),sQuery(id+"F0.wireOp",EDGE,"E2"),sQuery(id+"F0.wireOp",EDGE,"E3"),sQuery(id+"F0.wireOp",EDGE,"E4"),subQ0,sQuery(id+"F0.wireOp",EDGE,"E6"),sQuery(id+"F0.wireOp",EDGE,"E7"),sQuery(id+"F0.wireOp",EDGE,"E8"),sQuery(id+"F0.wireOp",EDGE,"E9"),sQuery(id+"F0.wireOp",EDGE,"E10"),sQuery(id+"F0.wireOp",EDGE,"E11"),sQuery(id+"F0.wireOp",EDGE,"E12"),sQuery(id+"F0.wireOp",EDGE,"E13"),sQuery(id+"F0.wireOp",EDGE,"E14"),sQuery(id+"F0.wireOp",EDGE,"E15"),sQuery(id+"F0.wireOp",EDGE,"E16"),sQuery(id+"F0.wireOp",EDGE,"E17"),sQuery(id+"F0.wireOp",EDGE,"E18"),sQuery(id+"F0.wireOp",EDGE,"E19"),sQuery(id+"F0.wireOp",EDGE,"E20"),sQuery(id+"F0.wireOp",EDGE,"E21"),sQuery(id+"F0.wireOp",EDGE,"E22"),sQuery(id+"F0.wireOp",EDGE,"E23"),sQuery(id+"F0.wireOp",EDGE,"E24")])],"isStart":true})],"blendedInto":[makeQuery(id+"F1.opExtrude","CAP_FACE",FACE,{"disambiguationData":[OSD([subQ1,sQuery(id+"F0.wireOp",EDGE,"E1"),sQuery(id+"F0.wireOp",EDGE,"E2"),sQuery(id+"F0.wireOp",EDGE,"E3"),sQuery(id+"F0.wireOp",EDGE,"E4"),subQ0,sQuery(id+"F0.wireOp",EDGE,"E6"),sQuery(id+"F0.wireOp",EDGE,"E7"),sQuery(id+"F0.wireOp",EDGE,"E8"),sQuery(id+"F0.wireOp",EDGE,"E9"),sQuery(id+"F0.wireOp",EDGE,"E10"),sQuery(id+"F0.wireOp",EDGE,"E11"),sQuery(id+"F0.wireOp",EDGE,"E12"),sQuery(id+"F0.wireOp",EDGE,"E13"),sQuery(id+"F0.wireOp",EDGE,"E14"),sQuery(id+"F0.wireOp",EDGE,"E15"),sQuery(id+"F0.wireOp",EDGE,"E16"),sQuery(id+"F0.wireOp",EDGE,"E17"),sQuery(id+"F0.wireOp",EDGE,"E18"),sQuery(id+"F0.wireOp",EDGE,"E19"),sQuery(id+"F0.wireOp",EDGE,"E20"),sQuery(id+"F0.wireOp",EDGE,"E21"),sQuery(id+"F0.wireOp",EDGE,"E22"),sQuery(id+"F0.wireOp",EDGE,"E23"),sQuery(id+"F0.wireOp",EDGE,"E24")])],"isStart":true})]});}
            var Q25;
            {var subQ0=sQuery(id+"F0.wireOp",EDGE,"E5");var subQ1=sQuery(id+"F0.wireOp",EDGE,"E4");Q25=makeQuery(id+"F10.opFillet","BLEND_EDGE",EDGE,{"blendedFrom":[makeQuery(id+"F1.opExtrude","SWEPT_EDGE",EDGE,{"disambiguationData":[OSD([subQ1,subQ0])]}),makeQuery(id+"F1.opExtrude","CAP_FACE",FACE,{"disambiguationData":[OSD([sQuery(id+"F0.wireOp",EDGE,"E0"),sQuery(id+"F0.wireOp",EDGE,"E1"),sQuery(id+"F0.wireOp",EDGE,"E2"),sQuery(id+"F0.wireOp",EDGE,"E3"),subQ1,subQ0,sQuery(id+"F0.wireOp",EDGE,"E6"),sQuery(id+"F0.wireOp",EDGE,"E7"),sQuery(id+"F0.wireOp",EDGE,"E8"),sQuery(id+"F0.wireOp",EDGE,"E9"),sQuery(id+"F0.wireOp",EDGE,"E10"),sQuery(id+"F0.wireOp",EDGE,"E11"),sQuery(id+"F0.wireOp",EDGE,"E12"),sQuery(id+"F0.wireOp",EDGE,"E13"),sQuery(id+"F0.wireOp",EDGE,"E14"),sQuery(id+"F0.wireOp",EDGE,"E15"),sQuery(id+"F0.wireOp",EDGE,"E16"),sQuery(id+"F0.wireOp",EDGE,"E17"),sQuery(id+"F0.wireOp",EDGE,"E18"),sQuery(id+"F0.wireOp",EDGE,"E19"),sQuery(id+"F0.wireOp",EDGE,"E20"),sQuery(id+"F0.wireOp",EDGE,"E21"),sQuery(id+"F0.wireOp",EDGE,"E22"),sQuery(id+"F0.wireOp",EDGE,"E23"),sQuery(id+"F0.wireOp",EDGE,"E24")])],"isStart":false})],"blendedInto":[makeQuery(id+"F1.opExtrude","CAP_FACE",FACE,{"disambiguationData":[OSD([sQuery(id+"F0.wireOp",EDGE,"E0"),sQuery(id+"F0.wireOp",EDGE,"E1"),sQuery(id+"F0.wireOp",EDGE,"E2"),sQuery(id+"F0.wireOp",EDGE,"E3"),subQ1,subQ0,sQuery(id+"F0.wireOp",EDGE,"E6"),sQuery(id+"F0.wireOp",EDGE,"E7"),sQuery(id+"F0.wireOp",EDGE,"E8"),sQuery(id+"F0.wireOp",EDGE,"E9"),sQuery(id+"F0.wireOp",EDGE,"E10"),sQuery(id+"F0.wireOp",EDGE,"E11"),sQuery(id+"F0.wireOp",EDGE,"E12"),sQuery(id+"F0.wireOp",EDGE,"E13"),sQuery(id+"F0.wireOp",EDGE,"E14"),sQuery(id+"F0.wireOp",EDGE,"E15"),sQuery(id+"F0.wireOp",EDGE,"E16"),sQuery(id+"F0.wireOp",EDGE,"E17"),sQuery(id+"F0.wireOp",EDGE,"E18"),sQuery(id+"F0.wireOp",EDGE,"E19"),sQuery(id+"F0.wireOp",EDGE,"E20"),sQuery(id+"F0.wireOp",EDGE,"E21"),sQuery(id+"F0.wireOp",EDGE,"E22"),sQuery(id+"F0.wireOp",EDGE,"E23"),sQuery(id+"F0.wireOp",EDGE,"E24")])],"isStart":false})]});}
            var Q26;
            {var subQ0=sQuery(id+"F0.wireOp",EDGE,"E5");var subQ1=sQuery(id+"F0.wireOp",EDGE,"E4");Q26=makeQuery(id+"F10.opFillet","BLEND_EDGE",EDGE,{"blendedFrom":[makeQuery(id+"F1.opExtrude","SWEPT_EDGE",EDGE,{"disambiguationData":[OSD([subQ1,subQ0])]}),makeQuery(id+"F1.opExtrude","CAP_FACE",FACE,{"disambiguationData":[OSD([sQuery(id+"F0.wireOp",EDGE,"E0"),sQuery(id+"F0.wireOp",EDGE,"E1"),sQuery(id+"F0.wireOp",EDGE,"E2"),sQuery(id+"F0.wireOp",EDGE,"E3"),subQ1,subQ0,sQuery(id+"F0.wireOp",EDGE,"E6"),sQuery(id+"F0.wireOp",EDGE,"E7"),sQuery(id+"F0.wireOp",EDGE,"E8"),sQuery(id+"F0.wireOp",EDGE,"E9"),sQuery(id+"F0.wireOp",EDGE,"E10"),sQuery(id+"F0.wireOp",EDGE,"E11"),sQuery(id+"F0.wireOp",EDGE,"E12"),sQuery(id+"F0.wireOp",EDGE,"E13"),sQuery(id+"F0.wireOp",EDGE,"E14"),sQuery(id+"F0.wireOp",EDGE,"E15"),sQuery(id+"F0.wireOp",EDGE,"E16"),sQuery(id+"F0.wireOp",EDGE,"E17"),sQuery(id+"F0.wireOp",EDGE,"E18"),sQuery(id+"F0.wireOp",EDGE,"E19"),sQuery(id+"F0.wireOp",EDGE,"E20"),sQuery(id+"F0.wireOp",EDGE,"E21"),sQuery(id+"F0.wireOp",EDGE,"E22"),sQuery(id+"F0.wireOp",EDGE,"E23"),sQuery(id+"F0.wireOp",EDGE,"E24")])],"isStart":true})],"blendedInto":[makeQuery(id+"F1.opExtrude","CAP_FACE",FACE,{"disambiguationData":[OSD([sQuery(id+"F0.wireOp",EDGE,"E0"),sQuery(id+"F0.wireOp",EDGE,"E1"),sQuery(id+"F0.wireOp",EDGE,"E2"),sQuery(id+"F0.wireOp",EDGE,"E3"),subQ1,subQ0,sQuery(id+"F0.wireOp",EDGE,"E6"),sQuery(id+"F0.wireOp",EDGE,"E7"),sQuery(id+"F0.wireOp",EDGE,"E8"),sQuery(id+"F0.wireOp",EDGE,"E9"),sQuery(id+"F0.wireOp",EDGE,"E10"),sQuery(id+"F0.wireOp",EDGE,"E11"),sQuery(id+"F0.wireOp",EDGE,"E12"),sQuery(id+"F0.wireOp",EDGE,"E13"),sQuery(id+"F0.wireOp",EDGE,"E14"),sQuery(id+"F0.wireOp",EDGE,"E15"),sQuery(id+"F0.wireOp",EDGE,"E16"),sQuery(id+"F0.wireOp",EDGE,"E17"),sQuery(id+"F0.wireOp",EDGE,"E18"),sQuery(id+"F0.wireOp",EDGE,"E19"),sQuery(id+"F0.wireOp",EDGE,"E20"),sQuery(id+"F0.wireOp",EDGE,"E21"),sQuery(id+"F0.wireOp",EDGE,"E22"),sQuery(id+"F0.wireOp",EDGE,"E23"),sQuery(id+"F0.wireOp",EDGE,"E24")])],"isStart":true})]});}
            var Q27;
            {var subQ0=sQuery(id+"F0.wireOp",EDGE,"E5");var subQ1=sQuery(id+"F0.wireOp",EDGE,"E0");Q27=makeQuery(id+"F9.opFillet","BLEND_EDGE",EDGE,{"blendedFrom":[makeQuery(id+"F1.opExtrude","SWEPT_EDGE",EDGE,{"disambiguationData":[OSD([subQ1,subQ0])]}),makeQuery(id+"F1.opExtrude","CAP_FACE",FACE,{"disambiguationData":[OSD([subQ1,sQuery(id+"F0.wireOp",EDGE,"E1"),sQuery(id+"F0.wireOp",EDGE,"E2"),sQuery(id+"F0.wireOp",EDGE,"E3"),sQuery(id+"F0.wireOp",EDGE,"E4"),subQ0,sQuery(id+"F0.wireOp",EDGE,"E6"),sQuery(id+"F0.wireOp",EDGE,"E7"),sQuery(id+"F0.wireOp",EDGE,"E8"),sQuery(id+"F0.wireOp",EDGE,"E9"),sQuery(id+"F0.wireOp",EDGE,"E10"),sQuery(id+"F0.wireOp",EDGE,"E11"),sQuery(id+"F0.wireOp",EDGE,"E12"),sQuery(id+"F0.wireOp",EDGE,"E13"),sQuery(id+"F0.wireOp",EDGE,"E14"),sQuery(id+"F0.wireOp",EDGE,"E15"),sQuery(id+"F0.wireOp",EDGE,"E16"),sQuery(id+"F0.wireOp",EDGE,"E17"),sQuery(id+"F0.wireOp",EDGE,"E18"),sQuery(id+"F0.wireOp",EDGE,"E19"),sQuery(id+"F0.wireOp",EDGE,"E20"),sQuery(id+"F0.wireOp",EDGE,"E21"),sQuery(id+"F0.wireOp",EDGE,"E22"),sQuery(id+"F0.wireOp",EDGE,"E23"),sQuery(id+"F0.wireOp",EDGE,"E24")])],"isStart":false})],"blendedInto":[makeQuery(id+"F1.opExtrude","CAP_FACE",FACE,{"disambiguationData":[OSD([subQ1,sQuery(id+"F0.wireOp",EDGE,"E1"),sQuery(id+"F0.wireOp",EDGE,"E2"),sQuery(id+"F0.wireOp",EDGE,"E3"),sQuery(id+"F0.wireOp",EDGE,"E4"),subQ0,sQuery(id+"F0.wireOp",EDGE,"E6"),sQuery(id+"F0.wireOp",EDGE,"E7"),sQuery(id+"F0.wireOp",EDGE,"E8"),sQuery(id+"F0.wireOp",EDGE,"E9"),sQuery(id+"F0.wireOp",EDGE,"E10"),sQuery(id+"F0.wireOp",EDGE,"E11"),sQuery(id+"F0.wireOp",EDGE,"E12"),sQuery(id+"F0.wireOp",EDGE,"E13"),sQuery(id+"F0.wireOp",EDGE,"E14"),sQuery(id+"F0.wireOp",EDGE,"E15"),sQuery(id+"F0.wireOp",EDGE,"E16"),sQuery(id+"F0.wireOp",EDGE,"E17"),sQuery(id+"F0.wireOp",EDGE,"E18"),sQuery(id+"F0.wireOp",EDGE,"E19"),sQuery(id+"F0.wireOp",EDGE,"E20"),sQuery(id+"F0.wireOp",EDGE,"E21"),sQuery(id+"F0.wireOp",EDGE,"E22"),sQuery(id+"F0.wireOp",EDGE,"E23"),sQuery(id+"F0.wireOp",EDGE,"E24")])],"isStart":false})]});}
            fillet(context, id + "F12", {"entities" : qUnion([Q0, Q1, Q2, Q3, Q4, Q5, Q6, Q7, Q8, Q9, Q10, Q11, Q12, Q13, Q14, Q15, Q16, Q17, Q18, Q19, Q20, Q21, Q22, Q23, Q24, Q25, Q26, Q27]), "radius" : 1.2 * mm, "tangentPropagation" : true, "allowEdgeOverflow" : false});
        }
    });
